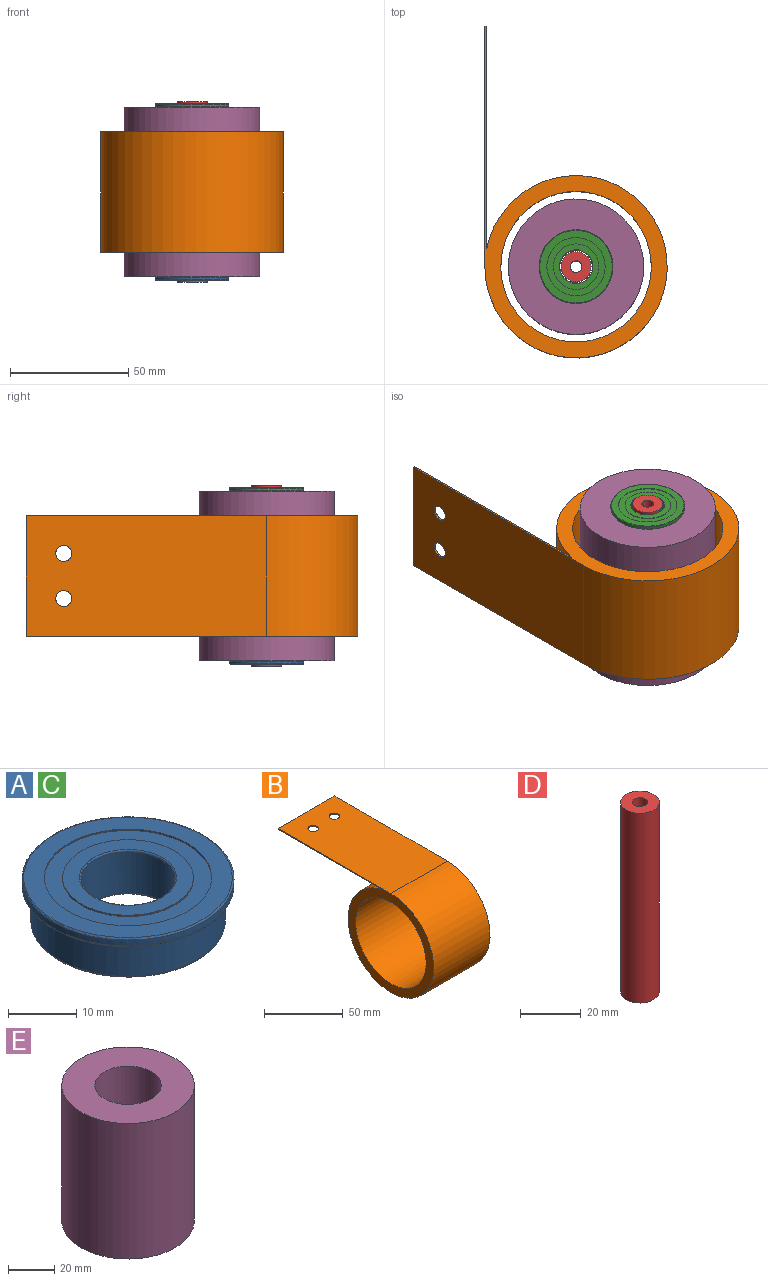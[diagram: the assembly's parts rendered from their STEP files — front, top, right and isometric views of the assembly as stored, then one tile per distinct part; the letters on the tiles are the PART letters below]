
ASSEMBLY  parts=5 mates=10
PART A: 21 faces, bbox 33.7x33.7x7.9 mm
  f0: torus R=14.29mm, axis (0,0,1), area 46.4mm2, adj f10,f17
  f1: torus R=15.31mm, axis (0,0,-1), area 38.2mm2, adj f9,f18
  f2: torus R=14.04mm, axis (0,0,1), area 35mm2, adj f11,f16
  f3: torus R=15.31mm, axis (0,0,1), area 38.2mm2, adj f9,f17
  f4: torus R=7.12mm, axis (0,0,-1), area 17.2mm2, adj f6,f20
  f5: torus R=7.12mm, axis (0,0,1), area 17.2mm2, adj f6,f14
  f6: cylinder r=6.88mm len=13.75mm, axis (0,0,1), area 321.3mm2, adj f4,f5
  f7: cylinder r=9.6mm len=19.2mm, axis (0,0,1), area 15.1mm2, adj f19,f20
  f8: cylinder r=12.29mm len=24.58mm, axis (0,0,1), area 19.3mm2, adj f18,f19
  f9: cylinder r=15.56mm len=31.12mm, axis (0,0,1), area 106.3mm2, adj f1,f3
  f10: cone r=14.29mm half-angle=30deg, axis (0,0,-1), area 38.6mm2, adj f0,f11
  f11: cylinder r=14.29mm len=28.58mm, axis (0,0,1), area 480.3mm2, adj f2,f10
  f12: cylinder r=12.29mm len=24.58mm, axis (0,0,1), area 19.3mm2, adj f15,f16
  f13: cylinder r=9.6mm len=19.2mm, axis (0,0,1), area 15.1mm2, adj f14,f15
  f14: plane 19.2x19.2mm, normal (0,0,-1), area 130.2mm2, adj f5,f13
  f15: plane 24.58x24.58mm, normal (0,0,-1), area 184.7mm2, adj f12,f13
  f16: plane 28.08x28.08mm, normal (0,0,-1), area 144.7mm2, adj f2,f12
  f17: plane 30.62x30.62mm, normal (0,0,-1), area 95.1mm2, adj f0,f3
  f18: plane 30.62x30.62mm, normal (0,0,1), area 262.1mm2, adj f1,f8
  f19: plane 24.58x24.58mm, normal (0,0,1), area 184.7mm2, adj f7,f8
  f20: plane 19.2x19.2mm, normal (0,0,1), area 130.2mm2, adj f4,f7
PART B: 9 faces, bbox 50.8x140.1x77 mm
  f0: cylinder r=3.37mm len=6.73mm, axis (0,0,1), area 16.7mm2, adj f6,f8
  f1: cylinder r=3.37mm len=6.73mm, axis (0,0,1), area 16.7mm2, adj f6,f8
  f2: cylinder r=31.75mm len=63.5mm, axis (-1,0,0), area 10134.1mm2, adj f4,f5
  f3: cylinder r=38.48mm len=76.96mm, axis (-1,0,0), area 11886.5mm2, adj f4,f5,f6,f8
  f4: plane 140.08x76.96mm, normal (1,0,0), area 1561mm2, adj f2,f3,f6,f7,f8
  f5: plane 140.08x76.96mm, normal (-1,0,0), area 1561mm2, adj f2,f3,f6,f7,f8
  f6: plane 93.86x50.8mm, normal (0,0,-1), area 4696.7mm2, adj f0,f1,f3,f4,f5,f7
  f7: plane 50.8x0.79mm, normal (0,1,0), area 40mm2, adj f4,f5,f6,f8
  f8: plane 101.6x50.8mm, normal (0,0,1), area 5090.1mm2, adj f0,f1,f3,f4,f5,f7
PART C: same geometry as A
PART D: 4 faces, bbox 12.7x12.7x76.2 mm
  f0: cylinder r=2.48mm len=76.2mm, axis (0,0,-1), area 1185.7mm2, adj f2,f3
  f1: cylinder r=6.35mm len=76.2mm, axis (0,0,-1), area 3040.2mm2, adj f2,f3
  f2: plane 12.7x12.7mm, normal (0,0,1), area 107.4mm2, adj f0,f1
  f3: plane 12.7x12.7mm, normal (0,0,-1), area 107.4mm2, adj f0,f1
PART E: 4 faces, bbox 57.2x57.2x71.4 mm
  f0: cylinder r=14.29mm len=71.44mm, axis (0,0,-1), area 6413mm2, adj f2,f3
  f1: cylinder r=28.57mm len=71.44mm, axis (0,0,-1), area 12826mm2, adj f2,f3
  f2: plane 57.15x57.15mm, normal (0,0,1), area 1923.9mm2, adj f0,f1
  f3: plane 57.15x57.15mm, normal (0,0,-1), area 1923.9mm2, adj f0,f1
PLACE A rot(axis=(1,0,0),180deg) t=(-4.53,13.13,-9.58)mm
PLACE B rot(axis=(0,-1,0),90deg) t=(-4.53,13.13,23.72)mm
PLACE C t=(-4.53,13.13,57.09)mm
PLACE D t=(-4.53,13.13,-14.38)mm
PLACE E t=(-4.53,13.13,-11.96)mm fixed
MATE cylindrical B.f2 <-> D.f0  axis (0,0,-1) through (-4.53,13.13,23.72)mm
MATE cylindrical D.f0 <-> C.f0  axis (0,0,-1) through (-4.53,13.13,23.72)mm
MATE planar B.f5 <-> D.f0  axis (0,0,-1) through (-6.38,15.73,-1.68)mm
MATE planar A.f0 <-> E.f0  axis (0,0,1) through (-4.53,13.13,-11.96)mm
MATE cylindrical A.f0 <-> E.f0  axis (0,0,1) through (-4.53,13.13,-11.96)mm
MATE planar C.f0 <-> E.f0  axis (0,0,-1) through (-4.53,13.13,59.47)mm
MATE planar D.f0 <-> C.f0  axis (0,0,1) through (-4.53,13.13,61.82)mm
MATE cylindrical C.f0 <-> E.f0  axis (0,0,1) through (-4.53,13.13,61.06)mm
MATE planar D.f0 <-> A.f0  axis (0,0,-1) through (-4.53,13.13,-14.38)mm
MATE planar D.f0 <-> A.f0  axis (0,0,-1) through (-4.53,13.13,-14.38)mm
